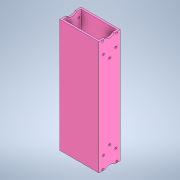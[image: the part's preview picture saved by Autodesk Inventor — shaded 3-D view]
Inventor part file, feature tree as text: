
AUTODESK INVENTOR PART (.ipt)
format: ipt  version: 2022 (Build 260153000, 153)  size: 241,152 bytes
history: native  units: mm
features: other x15, sketch x7, extrude x6, projected_geometry x3, mirror x1, loft x1, pattern_circular x1
ambient origin geometry x8: Origin, YZ Plane, XZ Plane, XY Plane, X Axis, Y Axis, Z Axis, Center Point
bodies: Body1 (feature_tree)
feature tree (34):
  other  "Твердое тело1"
  extrude  "Выдавливание1"  Depth=40.2mm
  extrude  "Выдавливание3"  Depth=20.0mm
  extrude  "Выдавливание4"  Depth=2.0mm
  extrude  "Выдавливание2"  Depth=2.0mm
  other  "РабПлоскость3"
  extrude  "Выдавливание5"  Depth=24.75mm TaperAngle=0.0deg
  other  "РабПлоскость5"
  mirror  "Зеркальное отражение2"
  extrude  "Выдавливание6"  Depth=2.0mm TaperAngle=0.0deg
  other  "РабПлоскость1"
  loft  "Лофт1"
  other  "РабОсь6"
  other  "РабПлоскость4"
  other  "РабТочка2"
  other  "РабОсь10"
  pattern_circular  "Круговой массив1"  [2 undecoded]
  sketch  "Эскиз2"
  sketch  "Эскиз3"
  sketch  "Эскиз4"
  projected_geometry  "Спроецированная петля1"
  sketch  "Эскиз5"
  projected_geometry  "Спроецированная петля2"
  sketch  "Эскиз6"
  other  "Ребра1"
  other  "РабОсь4"
  other  "РабОсь5"
  other  "РабТочка1"
  other  "РабОсь7"
  other  "РабОсь9"
  other  "РабТочка3"
  sketch  "Эскиз7"
  sketch  "Эскиз9"
  projected_geometry  "Спроецированная петля3"
note: 2 required parameter values undecoded (feature->parameter linkage not recoverable at this tier; creation-order binding heuristic only, values carry confidence <= 0.55)
